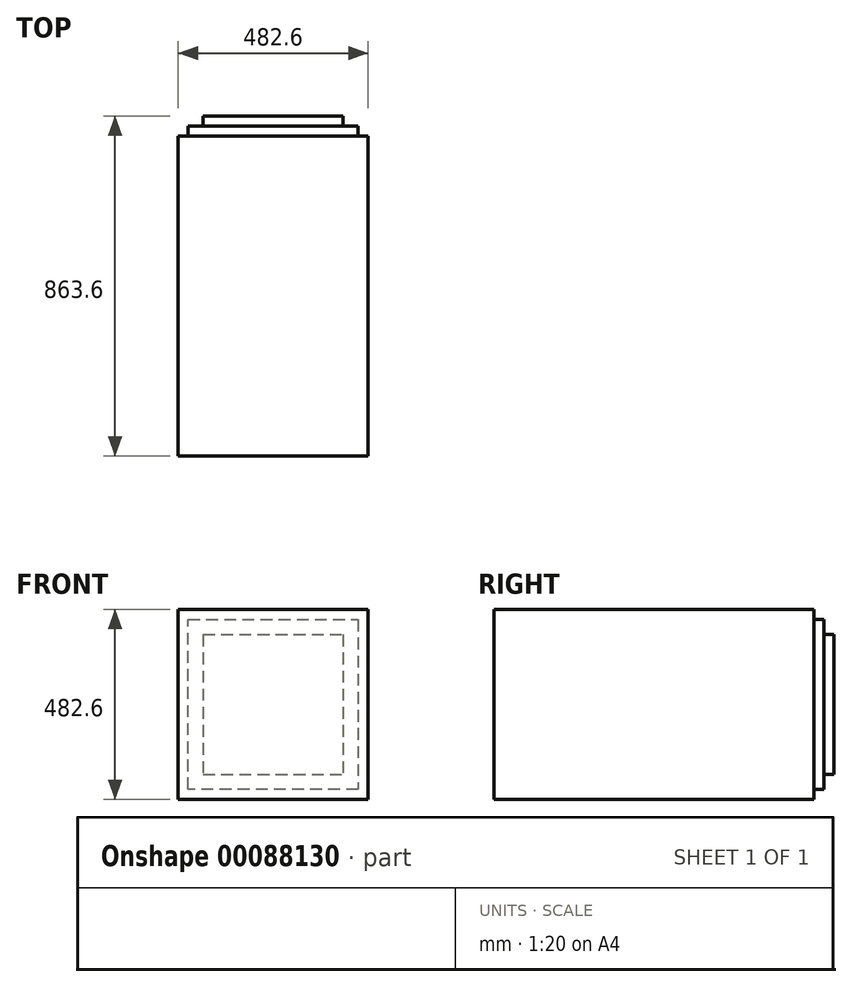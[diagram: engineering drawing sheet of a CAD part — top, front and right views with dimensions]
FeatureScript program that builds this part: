
annotation { "Feature Type Name" : "Feature", "Feature Type Description" : "" }
export const myFeature = defineFeature(function(context is Context, id is Id, definition is map)
    precondition{}
    {
        {
            var Q0;
            Q0=qCreatedBy(makeId("Top.planeOp"),FACE);
            var sketch = newSketch(context, id + "F0", { "sketchPlane" : qUnion([Q0])});
            skLineSegment(sketch, "E0.bottom", {"start": v(-688.12, 344.63) * mm, "end": v(-205.52, 344.63) * mm});
            skLineSegment(sketch, "E0.top", {"start": v(-688.12, -468.17) * mm, "end": v(-205.52, -468.17) * mm});
            skLineSegment(sketch, "E0.left", {"start": v(-688.12, 344.63) * mm, "end": v(-688.12, -468.17) * mm});
            skLineSegment(sketch, "E0.right", {"start": v(-205.52, 344.63) * mm, "end": v(-205.52, -468.17) * mm});
            skSolve(sketch);
        }
        {
            var Q0;
            Q0 = qSketchRegion(id + "F0", true);
            extrude(context, id + "F1", {"entities" : qUnion([Q0]), "depth" : 482.6 * mm});
        }
        {
            var Q0;
            Q0=makeQuery(id+"F1.opExtrude","SWEPT_FACE",FACE,{"disambiguationData":[OSD([sQuery(id+"F0.wireOp",EDGE,"E0.bottom")])]});
            var sketch = newSketch(context, id + "F2", { "sketchPlane" : qUnion([Q0])});
            skLineSegment(sketch, "E1.0", {"start": v(688.12, 482.6) * mm, "end": v(688.12, 0) * mm});
            skLineSegment(sketch, "E1.1", {"start": v(688.12, 0) * mm, "end": v(205.52, 0) * mm});
            skLineSegment(sketch, "E1.2", {"start": v(688.12, 482.6) * mm, "end": v(205.52, 482.6) * mm});
            skLineSegment(sketch, "E1.3", {"start": v(205.52, 482.6) * mm, "end": v(205.52, 0) * mm});
            skLineSegment(sketch, "E2.0", {"start": v(624.62, 419.1) * mm, "end": v(269.02, 419.1) * mm});
            skLineSegment(sketch, "E2.1", {"start": v(624.62, 419.1) * mm, "end": v(624.62, 63.5) * mm});
            skLineSegment(sketch, "E2.2", {"start": v(624.62, 63.5) * mm, "end": v(269.02, 63.5) * mm});
            skLineSegment(sketch, "E2.3", {"start": v(269.02, 419.1) * mm, "end": v(269.02, 63.5) * mm});
            skLineSegment(sketch, "E3.0", {"start": v(230.92, 25.4) * mm, "end": v(662.72, 25.4) * mm});
            skLineSegment(sketch, "E3.1", {"start": v(230.92, 457.2) * mm, "end": v(230.92, 25.4) * mm});
            skLineSegment(sketch, "E3.2", {"start": v(662.72, 457.2) * mm, "end": v(230.92, 457.2) * mm});
            skLineSegment(sketch, "E3.3", {"start": v(662.72, 25.4) * mm, "end": v(662.72, 457.2) * mm});
            skSolve(sketch);
        }
        {
            var Q0;
            Q0=makeQuery(id+"F2.imprint","IMPRINT",FACE,{"disambiguationData":[TD([[makeQuery(id+"F2.imprint","IMPRINT",EDGE,{"derivedFrom":sQuery(id+"F2.wireOp",EDGE,"E2.0")}),1.0]])]});
            extrude(context, id + "F3", {"entities" : qUnion([Q0]), "operationType" : NewBodyOperationType.ADD, "depth" : 50.8 * mm});
        }
        {
            var Q0;
            Q0=makeQuery(id+"F2.imprint","IMPRINT",FACE,{"disambiguationData":[TD([[makeQuery(id+"F2.imprint","IMPRINT",EDGE,{"derivedFrom":sQuery(id+"F2.wireOp",EDGE,"E2.0")}),-1.0]])]});
            extrude(context, id + "F4", {"entities" : qUnion([Q0]), "operationType" : NewBodyOperationType.ADD, "depth" : 25.4 * mm});
        }
    });
